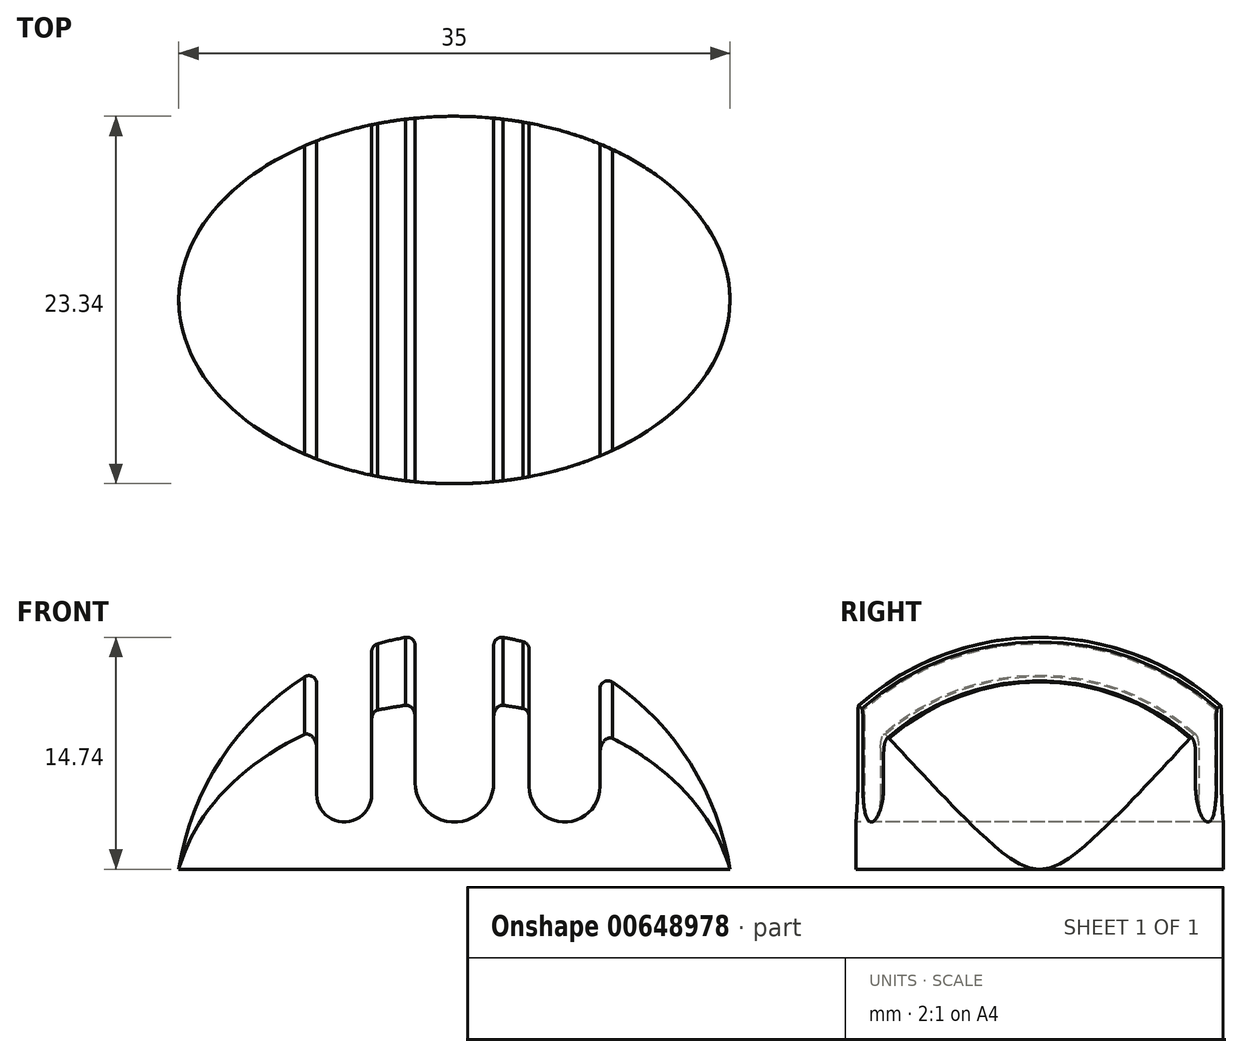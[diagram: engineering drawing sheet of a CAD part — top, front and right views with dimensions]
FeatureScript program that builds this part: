
annotation { "Feature Type Name" : "Feature", "Feature Type Description" : "" }
export const myFeature = defineFeature(function(context is Context, id is Id, definition is map)
    precondition{}
    {
        {
            assignVariable(context, id + "F0", {"name" : "fillet", "anyValue" : 0.5 * mm});
        }
        {
            var Q0;
            Q0=qCreatedBy(makeId("Front.planeOp"),FACE);
            var sketch = newSketch(context, id + "F1", { "sketchPlane" : qUnion([Q0])});
            skLineSegment(sketch, "E0", {"start": v(-17.5, 0) * mm, "end": v(17.5, 0) * mm});
            skArc(sketch, "E1", {"start": v(17.5, 0) * mm, "mid": v(0, 15) * mm, "end": v(-17.5, 0) * mm});
            skLineSegment(sketch, "E2", {"start": v(0, 0) * mm, "end": v(0, 15) * mm});
            skSolve(sketch);
        }
        {
            var Q0;
            {var subQ3=sQuery(id+"F1.wireOp",EDGE,"E2");Q0=makeQuery(id+"F1.imprint","IMPRINT",FACE,{"disambiguationData":[TD([[makeQuery(id+"F1.imprint","IMPRINT",EDGE,{"derivedFrom":subQ3}),1.0]])]});}
            var Q1;
            Q1=sQuery(id+"F1.wireOp",EDGE,"E2");
            revolve(context, id + "F2", {"entities" : qUnion([Q0]), "axis" : qUnion([Q1]), "revolveType" : RevolveType.FULL});
        }
        {
            var Q0;
            Q0=qCreatedBy(makeId("Front.planeOp"),FACE);
            var sketch = newSketch(context, id + "F3", { "sketchPlane" : qUnion([Q0])});
            skLineSegment(sketch, "E3", {"start": v(-16.76, 3) * mm, "end": v(16.76, 3) * mm});
            skCircle(sketch, "E4", {"center": v(-7, 4.75) * mm, "radius": 1.75 * mm});
            skCircle(sketch, "E5", {"center": v(7, 5.25) * mm, "radius": 2.25 * mm});
            skLineSegment(sketch, "E6.bottom", {"start": v(-5.25, 4.75) * mm, "end": v(-8.75, 4.75) * mm});
            skLineSegment(sketch, "E6.top", {"start": v(-5.25, 14.2) * mm, "end": v(-8.75, 14.2) * mm});
            skLineSegment(sketch, "E6.left", {"start": v(-5.25, 4.75) * mm, "end": v(-5.25, 14.2) * mm});
            skLineSegment(sketch, "E6.right", {"start": v(-8.75, 4.75) * mm, "end": v(-8.75, 14.2) * mm});
            skPoint(sketch, "E6.middle", {"position": v(-7, 9.48) * mm});
            skLineSegment(sketch, "E7.bottom", {"start": v(9.25, 5.25) * mm, "end": v(4.75, 5.25) * mm});
            skLineSegment(sketch, "E7.top", {"start": v(9.25, 14.35) * mm, "end": v(4.75, 14.35) * mm});
            skLineSegment(sketch, "E7.left", {"start": v(9.25, 5.25) * mm, "end": v(9.25, 14.35) * mm});
            skLineSegment(sketch, "E7.right", {"start": v(4.75, 5.25) * mm, "end": v(4.75, 14.35) * mm});
            skPoint(sketch, "E7.middle", {"position": v(7, 9.8) * mm});
            skCircle(sketch, "E8", {"center": v(0, 5.5) * mm, "radius": 2.5 * mm});
            skLineSegment(sketch, "E9.bottom", {"start": v(2.5, 5.5) * mm, "end": v(-2.5, 5.5) * mm});
            skLineSegment(sketch, "E9.top", {"start": v(2.5, 15) * mm, "end": v(-2.5, 15) * mm});
            skLineSegment(sketch, "E9.left", {"start": v(-2.5, 5.5) * mm, "end": v(-2.5, 15) * mm});
            skLineSegment(sketch, "E9.right", {"start": v(2.5, 5.5) * mm, "end": v(2.5, 15) * mm});
            skPoint(sketch, "E9.middle", {"position": v(0, 10.25) * mm});
            skSolve(sketch);
        }
        {
            var Q0;
            Q0 = qSketchRegion(id + "F3", true);
            extrude(context, id + "F4", {"entities" : qUnion([Q0]), "operationType" : NewBodyOperationType.REMOVE, "endBound" : BoundingType.THROUGH_ALL, "oppositeDirection" : true, "depth" : 25 * mm, "offsetDistance" : 25 * mm, "hasSecondDirection" : true, "secondDirectionBound" : SecondDirectionBoundingType.THROUGH_ALL, "secondDirectionOppositeDirection" : false, "secondDirectionDepth" : 25 * mm});
        }
        {
            var Q0;
            Q0=qCreatedBy(makeId("Top.planeOp"),FACE);
            var sketch = newSketch(context, id + "F5", { "sketchPlane" : qUnion([Q0])});
            skEllipse(sketch, "E10", {"center": v(0, 0) * mm, "majorRadius": 17.5 * mm, "minorRadius": 11.67 * mm, "majorAxis": v(1, 0)});
            skSolve(sketch);
        }
        {
            var Q0;
            Q0 = qSketchRegion(id + "F5", true);
            extrude(context, id + "F6", {"entities" : qUnion([Q0]), "operationType" : NewBodyOperationType.INTERSECT, "endBound" : BoundingType.THROUGH_ALL, "depth" : 25 * mm, "offsetDistance" : 25 * mm});
        }
        {
            var Q0;
            Q0=makeQuery(id+"F4.boolean.opBoolean","INTERSECT",EDGE,{"disambiguationData":[OD(0.0)],"derivedFrom":[makeQuery(id+"F2.opRevolve","SWEPT_FACE",FACE,{"disambiguationData":[OSD([sQuery(id+"F1.wireOp",EDGE,"E1")])]}),makeQuery(id+"F4.opExtrude","SWEPT_FACE",FACE,{"disambiguationData":[OSD([sQuery(id+"F3.wireOp",EDGE,"E5")])]})]});
            var Q1;
            Q1=makeQuery(id+"F4.boolean.opBoolean","INTERSECT",EDGE,{"disambiguationData":[OD(0.0)],"derivedFrom":[makeQuery(id+"F2.opRevolve","SWEPT_FACE",FACE,{"disambiguationData":[OSD([sQuery(id+"F1.wireOp",EDGE,"E1")])]}),makeQuery(id+"F4.opExtrude","SWEPT_FACE",FACE,{"disambiguationData":[OSD([sQuery(id+"F3.wireOp",EDGE,"E4")])]})]});
            var Q2;
            Q2=makeQuery(id+"F4.boolean.opBoolean","INTERSECT",EDGE,{"derivedFrom":[makeQuery(id+"F2.opRevolve","SWEPT_FACE",FACE,{"disambiguationData":[OSD([sQuery(id+"F1.wireOp",EDGE,"E1")])]}),makeQuery(id+"F4.opExtrude","SWEPT_FACE",FACE,{"disambiguationData":[OSD([sQuery(id+"F3.wireOp",EDGE,"E9.left")])]})]});
            var Q3;
            Q3=makeQuery(id+"F4.boolean.opBoolean","INTERSECT",EDGE,{"derivedFrom":[makeQuery(id+"F2.opRevolve","SWEPT_FACE",FACE,{"disambiguationData":[OSD([sQuery(id+"F1.wireOp",EDGE,"E1")])]}),makeQuery(id+"F4.opExtrude","SWEPT_FACE",FACE,{"disambiguationData":[OSD([sQuery(id+"F3.wireOp",EDGE,"E9.right")])]})]});
            var Q4;
            Q4=makeQuery(id+"F4.boolean.opBoolean","INTERSECT",EDGE,{"derivedFrom":[makeQuery(id+"F2.opRevolve","SWEPT_FACE",FACE,{"disambiguationData":[OSD([sQuery(id+"F1.wireOp",EDGE,"E1")])]}),makeQuery(id+"F4.opExtrude","SWEPT_FACE",FACE,{"disambiguationData":[OSD([sQuery(id+"F3.wireOp",EDGE,"E7.right")])]})]});
            var Q5;
            Q5=makeQuery(id+"F4.boolean.opBoolean","INTERSECT",EDGE,{"derivedFrom":[makeQuery(id+"F2.opRevolve","SWEPT_FACE",FACE,{"disambiguationData":[OSD([sQuery(id+"F1.wireOp",EDGE,"E1")])]}),makeQuery(id+"F4.opExtrude","SWEPT_FACE",FACE,{"disambiguationData":[OSD([sQuery(id+"F3.wireOp",EDGE,"E7.left")])]})]});
            var Q6;
            Q6=makeQuery(id+"F4.boolean.opBoolean","INTERSECT",EDGE,{"derivedFrom":[makeQuery(id+"F2.opRevolve","SWEPT_FACE",FACE,{"disambiguationData":[OSD([sQuery(id+"F1.wireOp",EDGE,"E1")])]}),makeQuery(id+"F4.opExtrude","SWEPT_FACE",FACE,{"disambiguationData":[OSD([sQuery(id+"F3.wireOp",EDGE,"E6.left")])]})]});
            var Q7;
            Q7=makeQuery(id+"F4.boolean.opBoolean","INTERSECT",EDGE,{"derivedFrom":[makeQuery(id+"F2.opRevolve","SWEPT_FACE",FACE,{"disambiguationData":[OSD([sQuery(id+"F1.wireOp",EDGE,"E1")])]}),makeQuery(id+"F4.opExtrude","SWEPT_FACE",FACE,{"disambiguationData":[OSD([sQuery(id+"F3.wireOp",EDGE,"E6.right")])]})]});
            var Q8;
            Q8=makeQuery(id+"F6.boolean.opBoolean","INTERSECT",EDGE,{"disambiguationData":[OD(0.0)],"derivedFrom":[makeQuery(id+"F4.boolean.opBoolean","COPY",FACE,{"derivedFrom":makeQuery(id+"F4.opExtrude","SWEPT_FACE",FACE,{"disambiguationData":[OSD([sQuery(id+"F3.wireOp",EDGE,"E8")])]})}),makeQuery(id+"F6.boolean.toolComplement.opBoolean","COPY",FACE,{"derivedFrom":makeQuery(id+"F6.opExtrude","SWEPT_FACE",FACE,{"disambiguationData":[OSD([sQuery(id+"F5.wireOp",EDGE,"E10")])]})})]});
            var Q9;
            Q9=makeQuery(id+"F6.boolean.opBoolean","INTERSECT",EDGE,{"disambiguationData":[OD(0.0)],"derivedFrom":[makeQuery(id+"F4.boolean.opBoolean","COPY",FACE,{"derivedFrom":makeQuery(id+"F4.opExtrude","SWEPT_FACE",FACE,{"disambiguationData":[OSD([sQuery(id+"F3.wireOp",EDGE,"E4")])]})}),makeQuery(id+"F6.boolean.toolComplement.opBoolean","COPY",FACE,{"derivedFrom":makeQuery(id+"F6.opExtrude","SWEPT_FACE",FACE,{"disambiguationData":[OSD([sQuery(id+"F5.wireOp",EDGE,"E10")])]})})]});
            var Q10;
            Q10=makeQuery(id+"F6.boolean.opBoolean","INTERSECT",EDGE,{"disambiguationData":[OD(0.0)],"derivedFrom":[makeQuery(id+"F4.boolean.opBoolean","COPY",FACE,{"derivedFrom":makeQuery(id+"F4.opExtrude","SWEPT_FACE",FACE,{"disambiguationData":[OSD([sQuery(id+"F3.wireOp",EDGE,"E5")])]})}),makeQuery(id+"F6.boolean.toolComplement.opBoolean","COPY",FACE,{"derivedFrom":makeQuery(id+"F6.opExtrude","SWEPT_FACE",FACE,{"disambiguationData":[OSD([sQuery(id+"F5.wireOp",EDGE,"E10")])]})})]});
            fillet(context, id + "F7", {"entities" : qUnion([Q0, Q1, Q2, Q3, Q4, Q5, Q6, Q7, Q8, Q9, Q10]), "radius" : getVariable(context, 'fillet'), "tangentPropagation" : true, "allowEdgeOverflow" : false});
        }
    });
